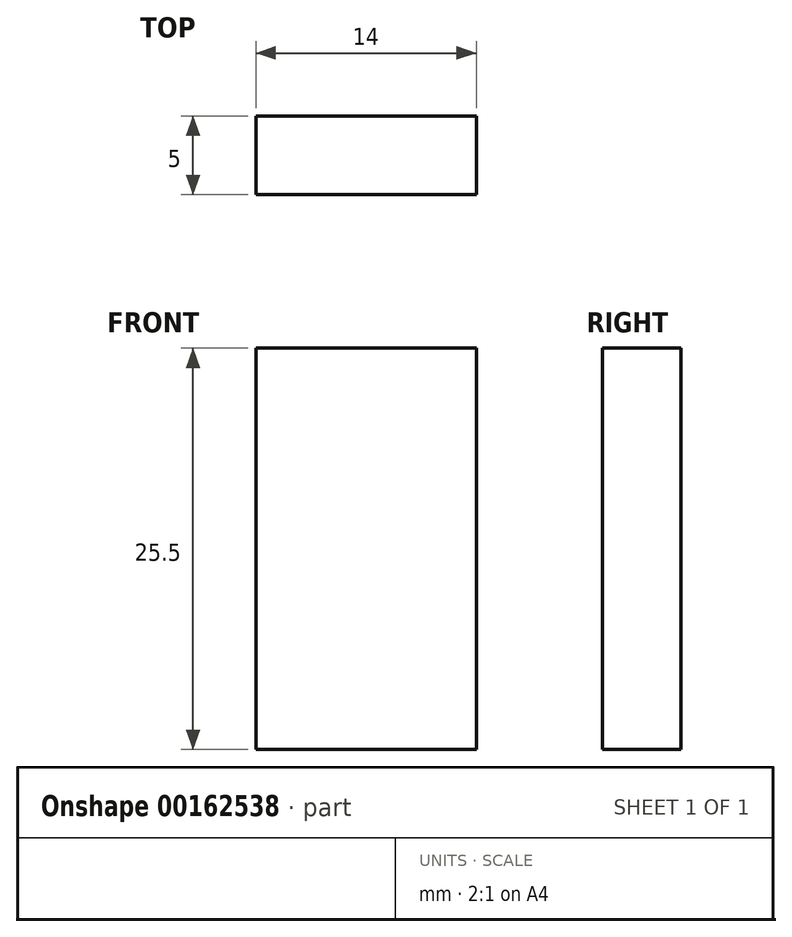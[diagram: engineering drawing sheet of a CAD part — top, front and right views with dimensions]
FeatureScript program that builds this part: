
annotation { "Feature Type Name" : "Feature", "Feature Type Description" : "" }
export const myFeature = defineFeature(function(context is Context, id is Id, definition is map)
    precondition{}
    {
        {
            var Q0;
            Q0=qCreatedBy(makeId("Front.planeOp"),FACE);
            var sketch = newSketch(context, id + "F0", { "sketchPlane" : qUnion([Q0])});
            skLineSegment(sketch, "E0.bottom", {"start": v(7, 12.75) * mm, "end": v(-7, 12.75) * mm});
            skLineSegment(sketch, "E0.top", {"start": v(7, -12.75) * mm, "end": v(-7, -12.75) * mm});
            skLineSegment(sketch, "E0.left", {"start": v(7, 12.75) * mm, "end": v(7, -12.75) * mm});
            skLineSegment(sketch, "E0.right", {"start": v(-7, 12.75) * mm, "end": v(-7, -12.75) * mm});
            skPoint(sketch, "E0.middle", {"position": v(0, 0) * mm});
            skSolve(sketch);
        }
        {
            var Q0;
            Q0=makeQuery(id+"F0.imprint","IMPRINT",FACE,{"disambiguationData":[TD([[makeQuery(id+"F0.imprint","IMPRINT",EDGE,{"derivedFrom":sQuery(id+"F0.wireOp",EDGE,"E0.bottom")}),1.0]])]});
            extrude(context, id + "F1", {"entities" : qUnion([Q0]), "depth" : 5 * mm});
        }
    });
